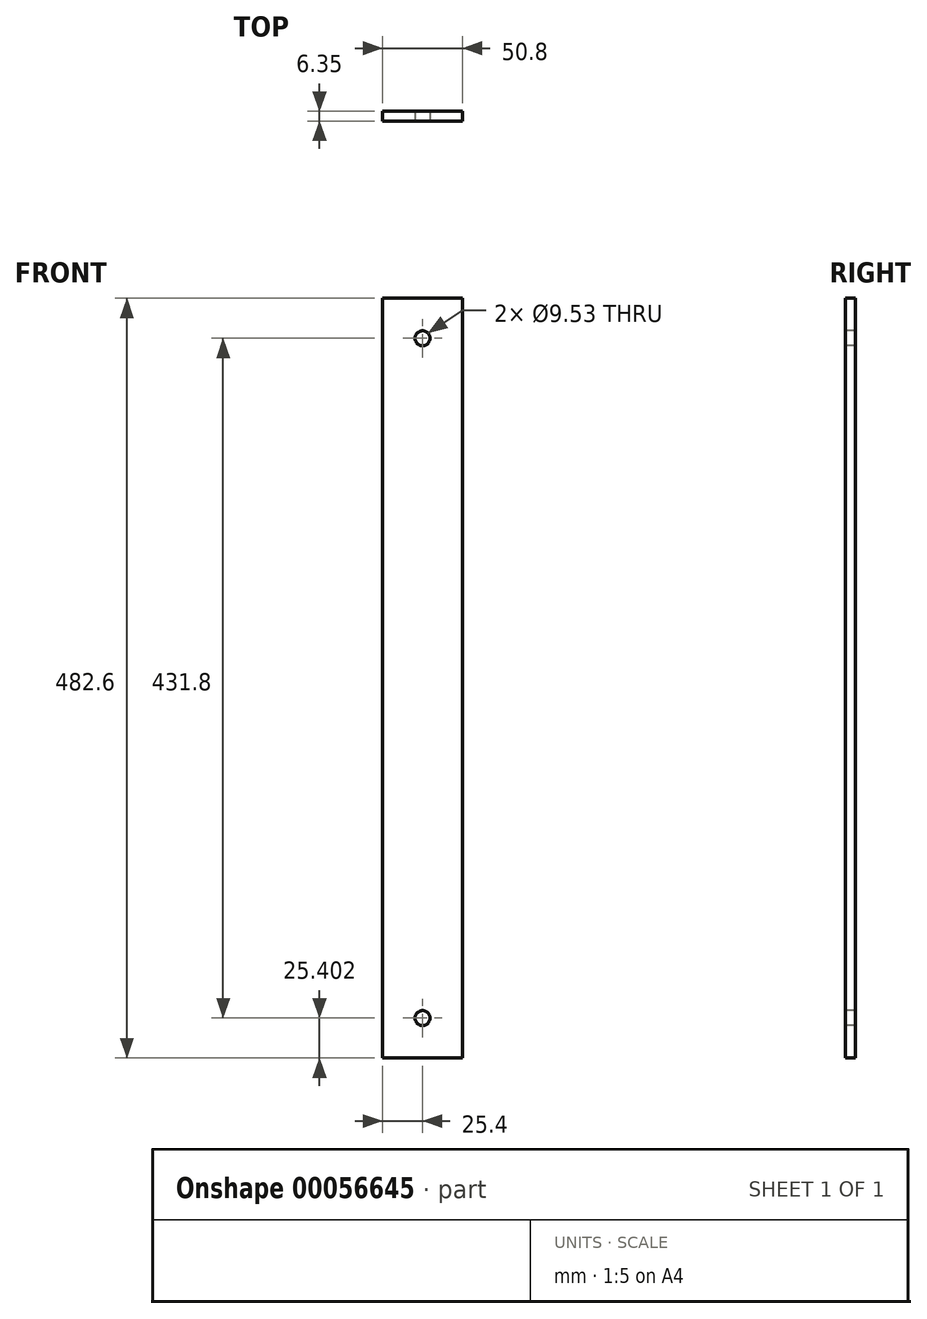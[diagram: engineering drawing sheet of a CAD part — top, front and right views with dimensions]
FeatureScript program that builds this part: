
annotation { "Feature Type Name" : "Feature", "Feature Type Description" : "" }
export const myFeature = defineFeature(function(context is Context, id is Id, definition is map)
    precondition{}
    {
        {
            var Q0;
            Q0=qCreatedBy(makeId("Right.planeOp"),FACE);
            var sketch = newSketch(context, id + "F0", { "sketchPlane" : qUnion([Q0])});
            skLineSegment(sketch, "E0.bottom", {"start": v(-36.23, 235.76) * mm, "end": v(-29.88, 235.76) * mm});
            skLineSegment(sketch, "E0.top", {"start": v(-36.23, -246.84) * mm, "end": v(-29.88, -246.84) * mm});
            skLineSegment(sketch, "E0.left", {"start": v(-36.23, 235.76) * mm, "end": v(-36.23, -246.84) * mm});
            skLineSegment(sketch, "E0.right", {"start": v(-29.88, 235.76) * mm, "end": v(-29.88, -246.84) * mm});
            skSolve(sketch);
        }
        {
            var Q0;
            Q0=qSketchRegion(id+"F0",true);
            extrude(context, id + "F1", {"entities" : qUnion([Q0]), "endBound" : BoundingType.SYMMETRIC, "depth" : 50.8 * mm});
        }
        {
            var Q0;
            Q0=makeQuery(id+"F1.opExtrude","SWEPT_FACE",FACE,{"disambiguationData":[OSD([sQuery(id+"F0.wireOp",EDGE,"E0.left")])]});
            var sketch = newSketch(context, id + "F2", { "sketchPlane" : qUnion([Q0])});
            skCircle(sketch, "E1", {"center": v(0, 210.36) * mm, "radius": 4.76 * mm});
            skPoint(sketch, "E1.centerSnap0", {"position": v(0, 235.76) * mm});
            skCircle(sketch, "E2", {"center": v(0, -221.44) * mm, "radius": 4.76 * mm});
            skSolve(sketch);
        }
        {
            var Q0;
            Q0=qSketchRegion(id+"F2",true);
            extrude(context, id + "F3", {"entities" : qUnion([Q0]), "operationType" : NewBodyOperationType.REMOVE, "endBound" : BoundingType.THROUGH_ALL, "oppositeDirection" : true, "depth" : 25.4 * mm});
        }
    });
